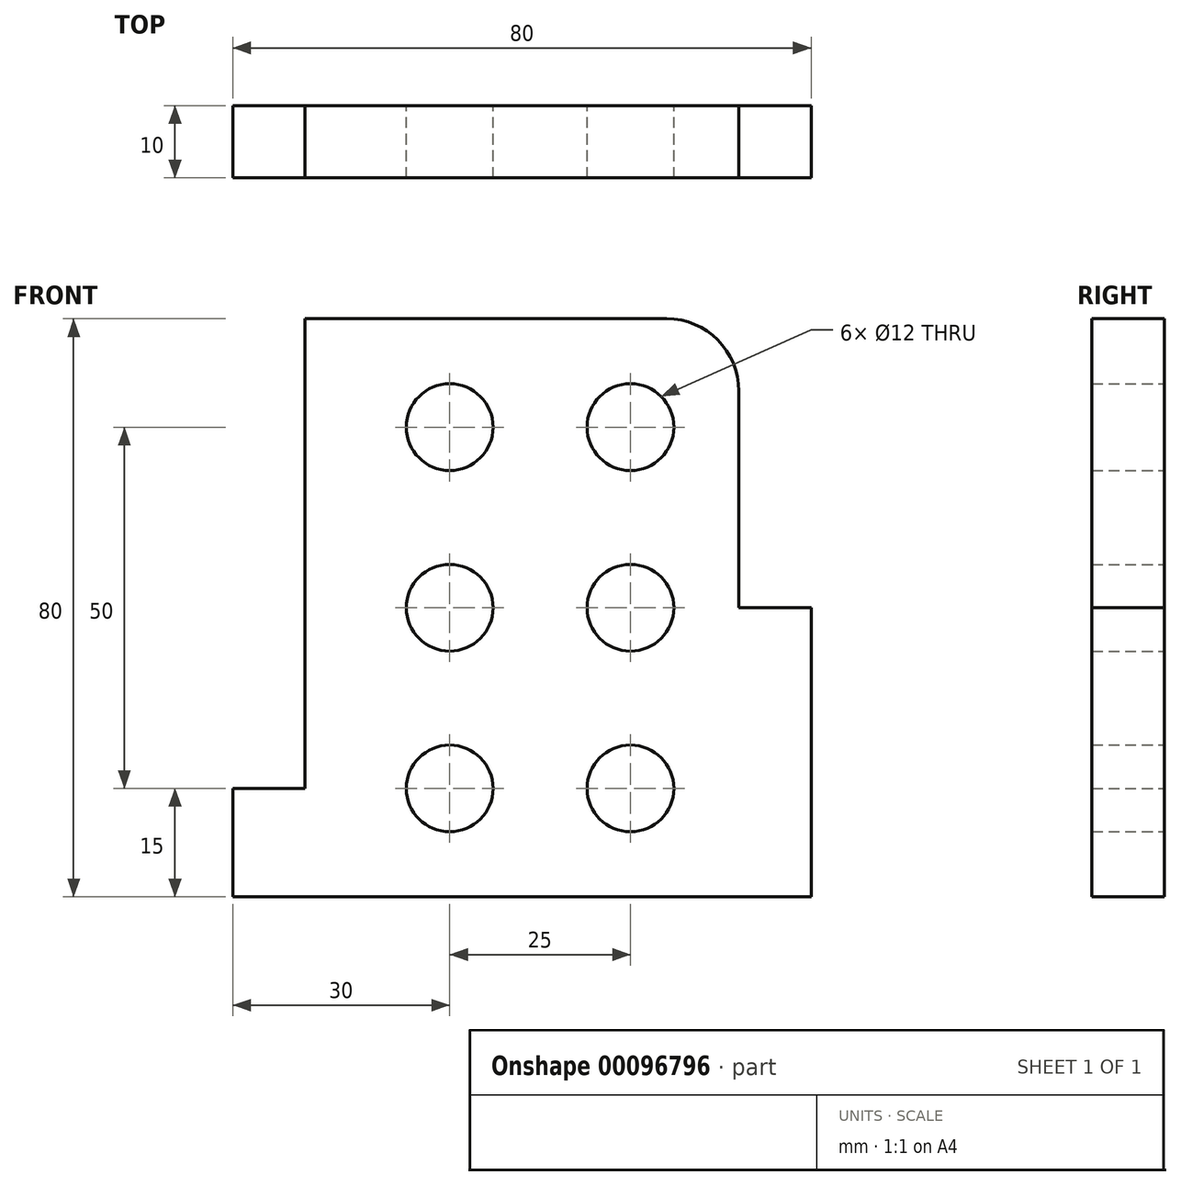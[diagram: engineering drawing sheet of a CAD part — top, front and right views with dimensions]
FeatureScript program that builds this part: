
annotation { "Feature Type Name" : "Feature", "Feature Type Description" : "" }
export const myFeature = defineFeature(function(context is Context, id is Id, definition is map)
    precondition{}
    {
        {
            var Q0;
            Q0=qCreatedBy(makeId("Front.planeOp"),FACE);
            var sketch = newSketch(context, id + "F0", { "sketchPlane" : qUnion([Q0])});
            skLineSegment(sketch, "E0", {"start": v(0, 0) * mm, "end": v(0, 15) * mm});
            skLineSegment(sketch, "E1", {"start": v(0, 15) * mm, "end": v(10, 15) * mm});
            skLineSegment(sketch, "E2", {"start": v(10, 15) * mm, "end": v(10, 80) * mm});
            skLineSegment(sketch, "E3", {"start": v(0, 0) * mm, "end": v(80, 0) * mm});
            skLineSegment(sketch, "E4", {"start": v(80, 0) * mm, "end": v(80, 40) * mm});
            skLineSegment(sketch, "E5", {"start": v(80, 40) * mm, "end": v(70, 40) * mm});
            skLineSegment(sketch, "E6", {"start": v(70, 40) * mm, "end": v(70, 70) * mm});
            skLineSegment(sketch, "E7", {"start": v(10, 80) * mm, "end": v(60, 80) * mm});
            skLineSegment(sketch, "E8", {"start": v(30, 72.62) * mm, "end": v(30, 7.38) * mm, "construction": true});
            skLineSegment(sketch, "E9", {"start": v(55, 74.05) * mm, "end": v(55, 5.95) * mm, "construction": true});
            skLineSegment(sketch, "E10", {"start": v(20.63, 65) * mm, "end": v(59.08, 65) * mm, "construction": true});
            skLineSegment(sketch, "E11", {"start": v(20.63, 40) * mm, "end": v(59.84, 40) * mm, "construction": true});
            skLineSegment(sketch, "E12", {"start": v(20.82, 15) * mm, "end": v(60.03, 15) * mm, "construction": true});
            skPoint(sketch, "E13.visualSharp", {"position": v(70, 80) * mm});
            skArc(sketch, "E13.filletArc", {"start": v(70, 70) * mm, "mid": v(67.07, 77.07) * mm, "end": v(60, 80) * mm});
            skCircle(sketch, "E14", {"center": v(30, 65) * mm, "radius": 6 * mm});
            skCircle(sketch, "E15", {"center": v(55, 65) * mm, "radius": 6 * mm});
            skCircle(sketch, "E16", {"center": v(30, 40) * mm, "radius": 6 * mm});
            skCircle(sketch, "E17", {"center": v(55, 40) * mm, "radius": 6 * mm});
            skCircle(sketch, "E18", {"center": v(30, 15) * mm, "radius": 6 * mm});
            skCircle(sketch, "E19", {"center": v(55, 15) * mm, "radius": 6 * mm});
            skSolve(sketch);
        }
        {
            var Q0;
            Q0 = qSketchRegion(id + "F0", true);
            extrude(context, id + "F1", {"entities" : qUnion([Q0]), "depth" : 10 * mm});
        }
    });
